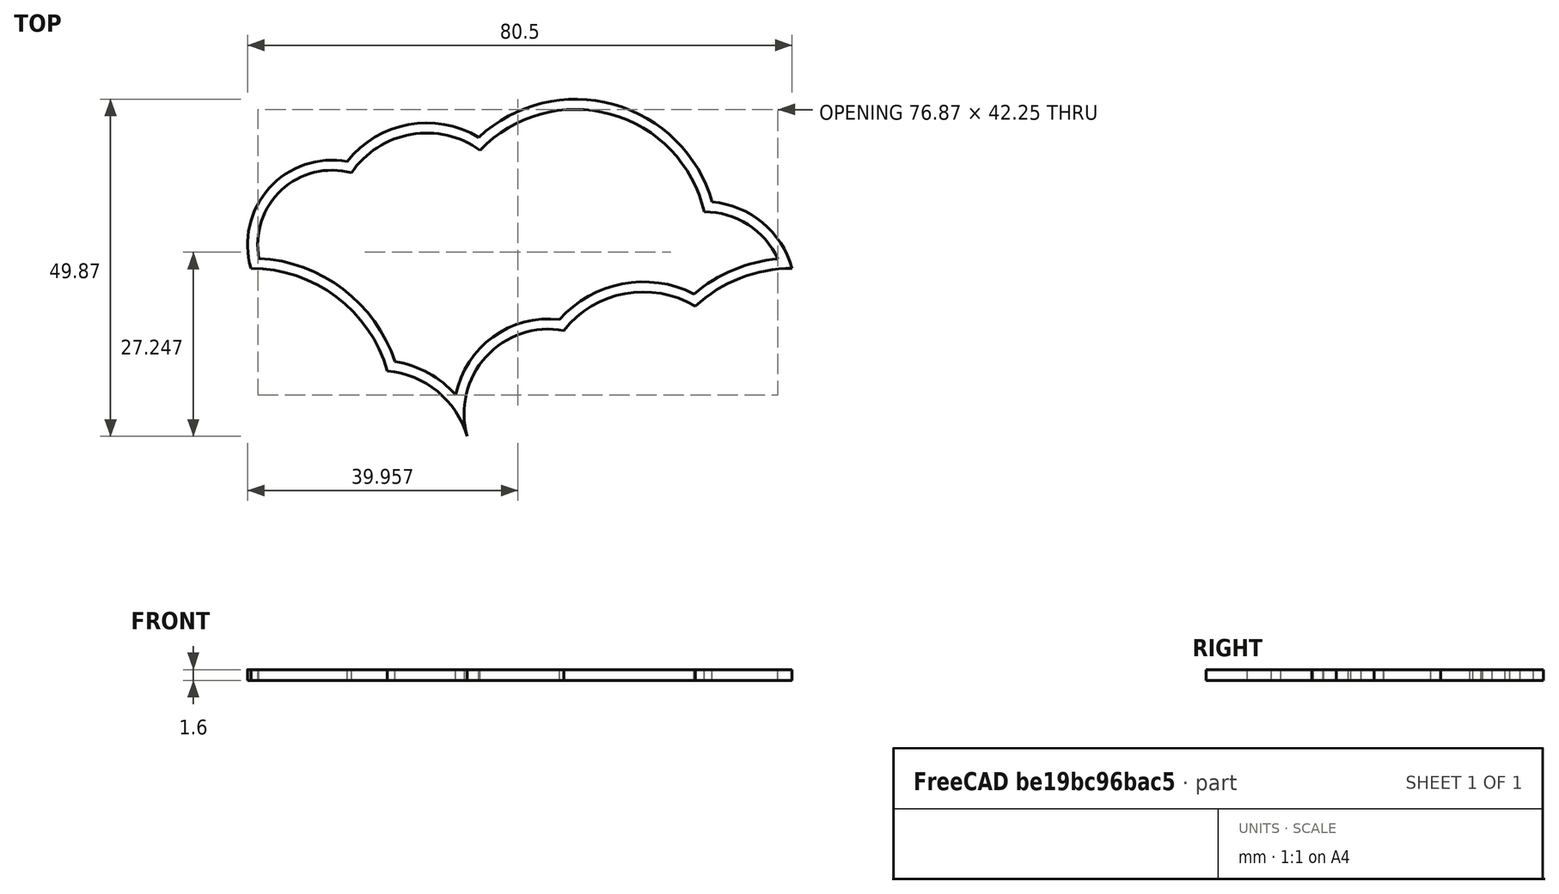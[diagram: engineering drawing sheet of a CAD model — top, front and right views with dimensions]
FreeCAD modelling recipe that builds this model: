
FCSTD DOCUMENT  (FreeCAD 0.16R6712 (Git))
Label: steam_badge
License: All rights reserved
LicenseURL: http://en.wikipedia.org/wiki/All_rights_reserved
objects: Part::Part2DObjectPython×3, Sketcher::SketchObject×1, PartDesign::Pad×1
note: 6 computed .brp shape members not serialized (recipe doc carries the construction recipe); baked Part::Feature solids carry a one-line shape summary decoded from their .brp

FEATURE [Sketcher::SketchObject] Sketch
  sketch-geometry (19):
    g0: ArcOfCircle CenterX=8 CenterY=4 CenterZ=0 NormalX=0 NormalY=0 NormalZ=1 Radius=21 StartAngle=0.280235 EndAngle=2.32012
    g1: ArcOfCircle CenterX=-28 CenterY=3.5 CenterZ=0 NormalX=0 NormalY=0 NormalZ=1 Radius=12.5 StartAngle=1.3914 EndAngle=3.42539
    g2: ArcOfCircle CenterX=27 CenterY=-3.64005 CenterZ=0 NormalX=0 NormalY=0 NormalZ=1 Radius=13.5 StartAngle=0.273013 EndAngle=1.48322
    g3: ArcOfCircle CenterX=-14 CenterY=6.5 CenterZ=0 NormalX=0 NormalY=0 NormalZ=1 Radius=15 StartAngle=1.03204 EndAngle=2.4729
    g4: LineSegment [constr] StartX=0 StartY=25 StartZ=0 EndX=8 EndY=25 EndZ=0
    g5: ArcOfCircle CenterX=-28 CenterY=3.5 CenterZ=0 NormalX=0 NormalY=0 NormalZ=1 Radius=11 StartAngle=1.30799 EndAngle=3.32734
    g6: ArcOfCircle CenterX=-14 CenterY=6.5 CenterZ=0 NormalX=0 NormalY=0 NormalZ=1 Radius=13.5 StartAngle=0.946866 EndAngle=2.54163
    g7: ArcOfCircle CenterX=8 CenterY=4 CenterZ=0 NormalX=0 NormalY=0 NormalZ=1 Radius=19.5 StartAngle=0.225493 EndAngle=2.38
    g8: ArcOfCircle CenterX=27 CenterY=-3.64005 CenterZ=0 NormalX=0 NormalY=0 NormalZ=1 Radius=12 StartAngle=0.433527 EndAngle=1.57027
    g9: ArcOfCircle CenterX=4 CenterY=-21.5 CenterZ=0 NormalX=0 NormalY=0 NormalZ=1 Radius=12.5 StartAngle=1.3914 EndAngle=3.41419
    g10: ArcOfCircle CenterX=18 CenterY=-18.5 CenterZ=0 NormalX=0 NormalY=0 NormalZ=1 Radius=15 StartAngle=1.03204 EndAngle=2.4729
    g11: ArcOfCircle CenterX=40 CenterY=-21 CenterZ=0 NormalX=0 NormalY=0 NormalZ=1 Radius=21 StartAngle=1.5708 EndAngle=2.32012
    g12: ArcOfCircle CenterX=-21 CenterY=-28.6401 CenterZ=0 NormalX=0 NormalY=0 NormalZ=1 Radius=13.5 StartAngle=0.283379 EndAngle=1.48322
    g13: ArcOfCircle CenterX=-40 CenterY=-21 CenterZ=0 NormalX=0 NormalY=0 NormalZ=1 Radius=21 StartAngle=0.280235 EndAngle=1.5708
    g14: ArcOfCircle CenterX=-40 CenterY=-21 CenterZ=0 NormalX=0 NormalY=0 NormalZ=1 Radius=22.5 StartAngle=0.324736 EndAngle=1.51792
    g15: ArcOfCircle CenterX=-21 CenterY=-28.6401 CenterZ=0 NormalX=0 NormalY=0 NormalZ=1 Radius=15 StartAngle=0.720345 EndAngle=1.41523
    g16: ArcOfCircle CenterX=4 CenterY=-21.5 CenterZ=0 NormalX=0 NormalY=0 NormalZ=1 Radius=14 StartAngle=1.45494 EndAngle=2.94354
    g17: ArcOfCircle CenterX=18 CenterY=-18.5 CenterZ=0 NormalX=0 NormalY=0 NormalZ=1 Radius=16.5 StartAngle=1.09932 EndAngle=2.41947
    g18: ArcOfCircle CenterX=40 CenterY=-21 CenterZ=0 NormalX=0 NormalY=0 NormalZ=1 Radius=22.5 StartAngle=1.66472 EndAngle=2.27142
  constraints (69):
    c: Coincident(g2,g0)
    c: DistanceY(g2,g-1) = 0
    c: DistanceX(g1,g-1) = 40
    c: DistanceX(g-1,g2) = 40
    c: DistanceY(g-1,g0) = 4
    c: DistanceY(g-1,g1) = 0
    c: DistanceX(g1,g-1) = 28
    c: DistanceX(g-1,g2) = 27
    c: Radius(g0) = 21
    c: DistanceX(g-1,g0) = 8
    c: Coincident(g3,g1)
    c: Coincident(g0,g3)
    c: DistanceX(g3,g-1) = 14
    c: DistanceY(g-1,g3) = 6.5
    c: Horizontal(g4)
    c: Tangent(g4,g0)
    c: DistanceX(g4,g-1) = 0
    c: DistanceX(g4,g4) = 8
    c: Coincident(g5,g1)
    c: Radius(g1) = 12.5
    c: Radius(g3) = 15
    c: Radius(g2) = 13.5
    c: Radius(g5) = 11
    c: Coincident(g6,g3)
    c: Radius(g6) = 13.5
    c: Coincident(g7,g0)
    c: Radius(g7) = 19.5
    c: Coincident(g8,g2)
    c: Radius(g8) = 12
    c: Coincident(g5,g6)
    c: Coincident(g6,g7)
    c: Coincident(g7,g8)
    c: DistanceX(g1,g9) = 32
    c: DistanceY(g9,g1) = 25
    c: Coincident(g10,g9)
    c: DistanceX(g3,g10) = 32
    c: DistanceY(g10,g3) = 25
    c: DistanceX(g0,g11) = 32
    c: DistanceY(g11,g0) = 25
    c: Radius(g9) = 12.5
    c: Radius(g10) = 15
    c: Radius(g11) = 21
    c: Coincident(g11,g10)
    c: PointOnObject(g11,g2)
    c: Radius(g12) = 13.5
    c: DistanceY(g12,g2) = 25
    c: DistanceX(g12,g2) = 48
    c: Coincident(g12,g9)
    c: Radius(g13) = 21
    c: DistanceY(g13,g0) = 25
    c: DistanceX(g13,g0) = 48
    c: Coincident(g13,g12)
    c: Coincident(g1,g13)
    c: Coincident(g13,g14)
    c: Radius(g14) = 22.5
    c: Coincident(g12,g15)
    c: Radius(g15) = 15
    c: Coincident(g14,g5)
    c: Coincident(g14,g15)
    c: Coincident(g9,g16)
    c: Radius(g16) = 14
    c: Coincident(g10,g17)
    c: Radius(g17) = 16.5
    c: Coincident(g15,g16)
    c: Coincident(g16,g17)
    c: Coincident(g11,g18)
    c: Radius(g18) = 22.5
    c: Coincident(g17,g18)
    c: Coincident(g8,g18)
FEATURE [Part::Part2DObjectPython] Clone2D  label="Clone of Sketch (2D)"  # Draft 2D object (typed FeaturePython)
  Objects = -> [Sketch]
  Placement = pos=(80,0,0) rot=(0,0,1;0rad)
  Scale = (1,1,1)
FEATURE [Part::Part2DObjectPython] Clone2D001  label="Clone of Sketch (2D)001"  # Draft 2D object (typed FeaturePython)
  Objects = -> [Sketch]
  Placement = pos=(32,-25,0) rot=(0,0,1;0rad)
  Scale = (1,1,1)
FEATURE [Part::Part2DObjectPython] Clone2D002  label="Clone of Sketch (2D)002"  # Draft 2D object (typed FeaturePython)
  Objects = -> [Sketch]
  Placement = pos=(112,-25,0) rot=(0,0,1;0rad)
  Scale = (1,1,1)
FEATURE [PartDesign::Pad] Pad
  Length = 1.6
  Length2 = 100
  Sketch = -> Sketch
  Type = 0
